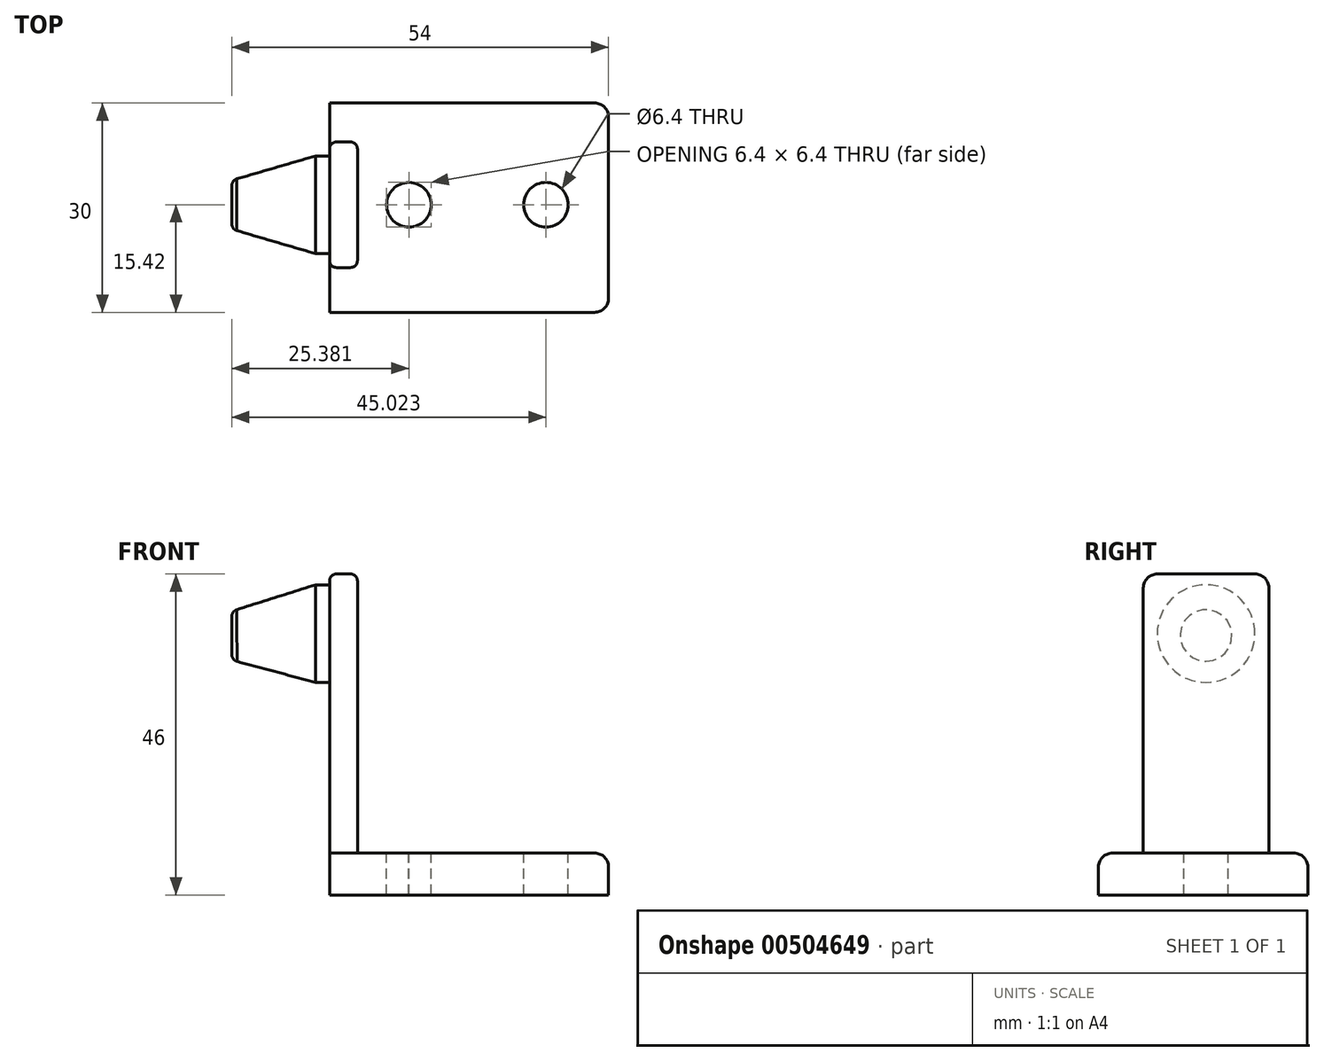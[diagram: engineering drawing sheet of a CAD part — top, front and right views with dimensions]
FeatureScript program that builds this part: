
annotation { "Feature Type Name" : "Feature", "Feature Type Description" : "" }
export const myFeature = defineFeature(function(context is Context, id is Id, definition is map)
    precondition{}
    {
        {
            var Q0;
            Q0=qCreatedBy(makeId("Top.planeOp"),FACE);
            var sketch = newSketch(context, id + "F0", { "sketchPlane" : qUnion([Q0])});
            skLineSegment(sketch, "E0.bottom", {"start": v(0, 14.58) * mm, "end": v(40, 14.58) * mm});
            skLineSegment(sketch, "E0.top", {"start": v(0, -15.42) * mm, "end": v(40, -15.42) * mm});
            skLineSegment(sketch, "E0.left", {"start": v(0, 14.58) * mm, "end": v(0, -15.42) * mm});
            skLineSegment(sketch, "E0.right", {"start": v(40, 14.58) * mm, "end": v(40, -15.42) * mm});
            skSolve(sketch);
        }
        {
            var Q0;
            Q0=qSketchRegion(id+"F0",true);
            extrude(context, id + "F1", {"entities" : qUnion([Q0]), "depth" : 6 * mm});
        }
        {
            var Q0;
            Q0=makeQuery(id+"F1.opExtrude","CAP_FACE",FACE,{"disambiguationData":[OSD([sQuery(id+"F0.wireOp",EDGE,"E0.bottom"),sQuery(id+"F0.wireOp",EDGE,"E0.top"),sQuery(id+"F0.wireOp",EDGE,"E0.left"),sQuery(id+"F0.wireOp",EDGE,"E0.right")])],"isStart":false});
            var sketch = newSketch(context, id + "F2", { "sketchPlane" : qUnion([Q0])});
            skLineSegment(sketch, "E1.bottom", {"start": v(0, 9) * mm, "end": v(4, 9) * mm});
            skLineSegment(sketch, "E1.top", {"start": v(0, -9) * mm, "end": v(4, -9) * mm});
            skLineSegment(sketch, "E1.left", {"start": v(0, 9) * mm, "end": v(0, -9) * mm});
            skLineSegment(sketch, "E1.right", {"start": v(4, 9) * mm, "end": v(4, -9) * mm});
            skSolve(sketch);
        }
        {
            var Q0;
            Q0=makeQuery(id+"F2.imprint","IMPRINT",FACE,{"disambiguationData":[TD([[makeQuery(id+"F2.imprint","IMPRINT",EDGE,{"derivedFrom":sQuery(id+"F2.wireOp",EDGE,"E1.bottom")}),-1.0]])]});
            extrude(context, id + "F3", {"entities" : qUnion([Q0]), "operationType" : NewBodyOperationType.ADD, "depth" : 40 * mm});
        }
        {
            var Q0;
            Q0=makeQuery(id+"F3.opExtrude","SWEPT_FACE",FACE,{"disambiguationData":[OSD([sQuery(id+"F2.wireOp",EDGE,"E1.right")])]});
            var sketch = newSketch(context, id + "F4", { "sketchPlane" : qUnion([Q0])});
            skLineSegment(sketch, "E2", {"start": v(0, 46) * mm, "end": v(0, 6) * mm, "construction": true});
            skLineSegment(sketch, "E3", {"start": v(-9, 37.45) * mm, "end": v(9, 37.45) * mm});
            skCircle(sketch, "E4", {"center": v(0, 37.45) * mm, "radius": 7 * mm});
            skSolve(sketch);
        }
        {
            var Q0;
            Q0=qSketchRegion(id+"F4",true);
            extrude(context, id + "F5", {"entities" : qUnion([Q0]), "operationType" : NewBodyOperationType.ADD, "oppositeDirection" : true, "depth" : 6 * mm});
        }
        {
            var Q0;
            Q0=makeQuery(id+"F5.opExtrude","CAP_FACE",FACE,{"disambiguationData":[OSD([sQuery(id+"F4.wireOp",EDGE,"E4")])],"isStart":false});
            cPlane(context, id + "F6", {"entities" : qUnion([Q0]), "cplaneType" : CPlaneType.OFFSET, "offset" : 12 * mm, "width" : 150 * mm, "height" : 150 * mm});
        }
        {
            var Q0;
            Q0=qCreatedBy(id+"F6.planeOp",FACE);
            var sketch = newSketch(context, id + "F7", { "sketchPlane" : qUnion([Q0])});
            skLineSegment(sketch, "E5", {"start": v(0, 37.17) * mm, "end": v(0, 37.17) * mm});
            skLineSegment(sketch, "E6", {"start": v(0, 37.17) * mm, "end": v(-8.55, 37.17) * mm, "construction": true});
            skCircle(sketch, "E7", {"center": v(0, 37.17) * mm, "radius": 3.5 * mm});
            skSolve(sketch);
        }
        {
            var Q0;
            Q0=makeQuery(id+"F5.opExtrude","CAP_FACE",FACE,{"disambiguationData":[OSD([sQuery(id+"F4.wireOp",EDGE,"E4")])],"isStart":false});
            var Q1;
            Q1=makeQuery(id+"F7.imprint","IMPRINT",FACE,{"disambiguationData":[TD([[makeQuery(id+"F7.imprint","IMPRINT",EDGE,{"derivedFrom":sQuery(id+"F7.wireOp",EDGE,"E7")}),1.0]])]});
            loft(context, id + "F8", {"sheetProfilesArray" : [{ "sheetProfileEntities" : qUnion([Q0]) }, { "sheetProfileEntities" : qUnion([Q1]) }]});
        }
        {
            var Q0;
            Q0=makeQuery(id+"F1.opExtrude","CAP_FACE",FACE,{"disambiguationData":[OSD([sQuery(id+"F0.wireOp",EDGE,"E0.bottom"),sQuery(id+"F0.wireOp",EDGE,"E0.top"),sQuery(id+"F0.wireOp",EDGE,"E0.left"),sQuery(id+"F0.wireOp",EDGE,"E0.right")])],"isStart":false});
            var sketch = newSketch(context, id + "F9", { "sketchPlane" : qUnion([Q0])});
            skCircle(sketch, "E8", {"center": v(11.38, 0) * mm, "radius": 3.2 * mm});
            skCircle(sketch, "E9", {"center": v(31.02, 0) * mm, "radius": 3.2 * mm});
            skLineSegment(sketch, "E10", {"start": v(11.34, 3.2) * mm, "end": v(31.02, 3.2) * mm});
            skLineSegment(sketch, "E11", {"start": v(11.67, -3.19) * mm, "end": v(31.02, -3.2) * mm});
            skSolve(sketch);
        }
        {
            var Q0;
            {var subQ0=sQuery(id+"F9.wireOp",EDGE,"E9");var subQ1=makeQuery(id+"F9.imprint","INTERSECT",VERTEX,{"derivedFrom":[subQ0,sQuery(id+"F9.wireOp",EDGE,"E10")]});Q0=makeQuery(id+"F9.imprint","IMPRINT",FACE,{"disambiguationData":[TD([[makeQuery(id+"F9.imprint","IMPRINT",EDGE,{"disambiguationData":[TD([[subQ1,-1.0]])],"derivedFrom":subQ0}),1.0]])]});}
            var Q1;
            {var subQ0=sQuery(id+"F9.wireOp",EDGE,"E10");Q1=makeQuery(id+"F9.imprint","IMPRINT",FACE,{"disambiguationData":[TD([[makeQuery(id+"F9.imprint","IMPRINT",EDGE,{"derivedFrom":subQ0}),-1.0]])]});}
            var Q2;
            {var subQ0=sQuery(id+"F9.wireOp",EDGE,"E8");var subQ2=makeQuery(id+"F9.imprint","IMPRINT",VERTEX,{"derivedFrom":subQ0});Q2=makeQuery(id+"F9.imprint","IMPRINT",FACE,{"disambiguationData":[TD([[makeQuery(id+"F9.imprint","IMPRINT",EDGE,{"disambiguationData":[TD([[subQ2,1.0]])],"derivedFrom":subQ0}),1.0]])]});}
            extrude(context, id + "F10", {"entities" : qUnion([Q0, Q1, Q2]), "operationType" : NewBodyOperationType.REMOVE, "endBound" : BoundingType.THROUGH_ALL, "oppositeDirection" : true, "depth" : 25 * mm});
        }
        {
            var Q0;
            Q0=makeQuery(id+"F3.opExtrude","CAP_EDGE",EDGE,{"disambiguationData":[OSD([sQuery(id+"F2.wireOp",EDGE,"E1.right")])],"isStart":false});
            var Q1;
            Q1=makeQuery(id+"F3.opExtrude","SWEPT_EDGE",EDGE,{"disambiguationData":[OSD([sQuery(id+"F2.wireOp",EDGE,"E1.top"),sQuery(id+"F2.wireOp",EDGE,"E1.right")])]});
            var Q2;
            Q2=makeQuery(id+"F3.opExtrude","SWEPT_EDGE",EDGE,{"disambiguationData":[OSD([sQuery(id+"F2.wireOp",EDGE,"E1.bottom"),sQuery(id+"F2.wireOp",EDGE,"E1.right")])]});
            var Q3;
            Q3=makeQuery(id+"F3.opExtrude","CAP_EDGE",EDGE,{"disambiguationData":[OSD([sQuery(id+"F2.wireOp",EDGE,"E1.right")])],"isStart":true});
            var Q4;
            {var subQ0=sQuery(id+"F2.wireOp",EDGE,"E1.top");var subQ1=sQuery(id+"F0.wireOp",EDGE,"E0.left");var subQ2=sQuery(id+"F2.wireOp",EDGE,"E1.left");Q4=makeQuery(id+"F5.boolean.opBoolean","SPLIT",EDGE,{"disambiguationData":[TD([makeQuery(id+"F1.opExtrude","CAP_FACE",FACE,{"disambiguationData":[OSD([sQuery(id+"F0.wireOp",EDGE,"E0.bottom"),sQuery(id+"F0.wireOp",EDGE,"E0.top"),subQ1,sQuery(id+"F0.wireOp",EDGE,"E0.right")])],"isStart":false})])],"derivedFrom":makeQuery(id+"F3.opExtrude","SWEPT_EDGE",EDGE,{"disambiguationData":[OSD([subQ1,subQ0,subQ2])]})});}
            var Q5;
            {var subQ0=sQuery(id+"F2.wireOp",EDGE,"E1.bottom");var subQ1=sQuery(id+"F0.wireOp",EDGE,"E0.left");var subQ2=sQuery(id+"F2.wireOp",EDGE,"E1.left");Q5=makeQuery(id+"F5.boolean.opBoolean","SPLIT",EDGE,{"disambiguationData":[TD([makeQuery(id+"F1.opExtrude","CAP_FACE",FACE,{"disambiguationData":[OSD([sQuery(id+"F0.wireOp",EDGE,"E0.bottom"),sQuery(id+"F0.wireOp",EDGE,"E0.top"),subQ1,sQuery(id+"F0.wireOp",EDGE,"E0.right")])],"isStart":false})])],"derivedFrom":makeQuery(id+"F3.opExtrude","SWEPT_EDGE",EDGE,{"disambiguationData":[OSD([subQ1,subQ0,subQ2])]})});}
            var Q6;
            Q6=makeQuery(id+"F3.opExtrude","CAP_EDGE",EDGE,{"disambiguationData":[OSD([sQuery(id+"F2.wireOp",EDGE,"E1.left")])],"isStart":false});
            var Q7;
            Q7=makeQuery(id+"F8.opLoft","MID_CAP_EDGE",EDGE,{"disambiguationData":[OSD([sQuery(id+"F4.wireOp",EDGE,"E4"),sQuery(id+"F7.wireOp",EDGE,"E7")])],"capPos":1.0});
            fillet(context, id + "F11", {"entities" : qUnion([Q0, Q1, Q2, Q3, Q4, Q5, Q6, Q7]), "radius" : 1 * mm, "tangentPropagation" : true, "allowEdgeOverflow" : false});
        }
        {
            var Q0;
            Q0=makeQuery(id+"F3.opExtrude","CAP_EDGE",EDGE,{"disambiguationData":[OSD([sQuery(id+"F2.wireOp",EDGE,"E1.bottom")])],"isStart":false});
            var Q1;
            Q1=makeQuery(id+"F3.opExtrude","CAP_EDGE",EDGE,{"disambiguationData":[OSD([sQuery(id+"F2.wireOp",EDGE,"E1.top")])],"isStart":false});
            var Q2;
            Q2=makeQuery(id+"F1.opExtrude","CAP_EDGE",EDGE,{"disambiguationData":[OSD([sQuery(id+"F0.wireOp",EDGE,"E0.top")])],"isStart":false});
            var Q3;
            Q3=makeQuery(id+"F1.opExtrude","CAP_EDGE",EDGE,{"disambiguationData":[OSD([sQuery(id+"F0.wireOp",EDGE,"E0.right")])],"isStart":false});
            var Q4;
            Q4=makeQuery(id+"F1.opExtrude","CAP_EDGE",EDGE,{"disambiguationData":[OSD([sQuery(id+"F0.wireOp",EDGE,"E0.bottom")])],"isStart":false});
            var Q5;
            Q5=makeQuery(id+"F1.opExtrude","SWEPT_EDGE",EDGE,{"disambiguationData":[OSD([sQuery(id+"F0.wireOp",EDGE,"E0.top"),sQuery(id+"F0.wireOp",EDGE,"E0.right")])]});
            var Q6;
            Q6=makeQuery(id+"F1.opExtrude","SWEPT_EDGE",EDGE,{"disambiguationData":[OSD([sQuery(id+"F0.wireOp",EDGE,"E0.bottom"),sQuery(id+"F0.wireOp",EDGE,"E0.right")])]});
            fillet(context, id + "F12", {"entities" : qUnion([Q0, Q1, Q2, Q3, Q4, Q5, Q6]), "radius" : 2 * mm, "tangentPropagation" : true, "allowEdgeOverflow" : false});
        }
    });
